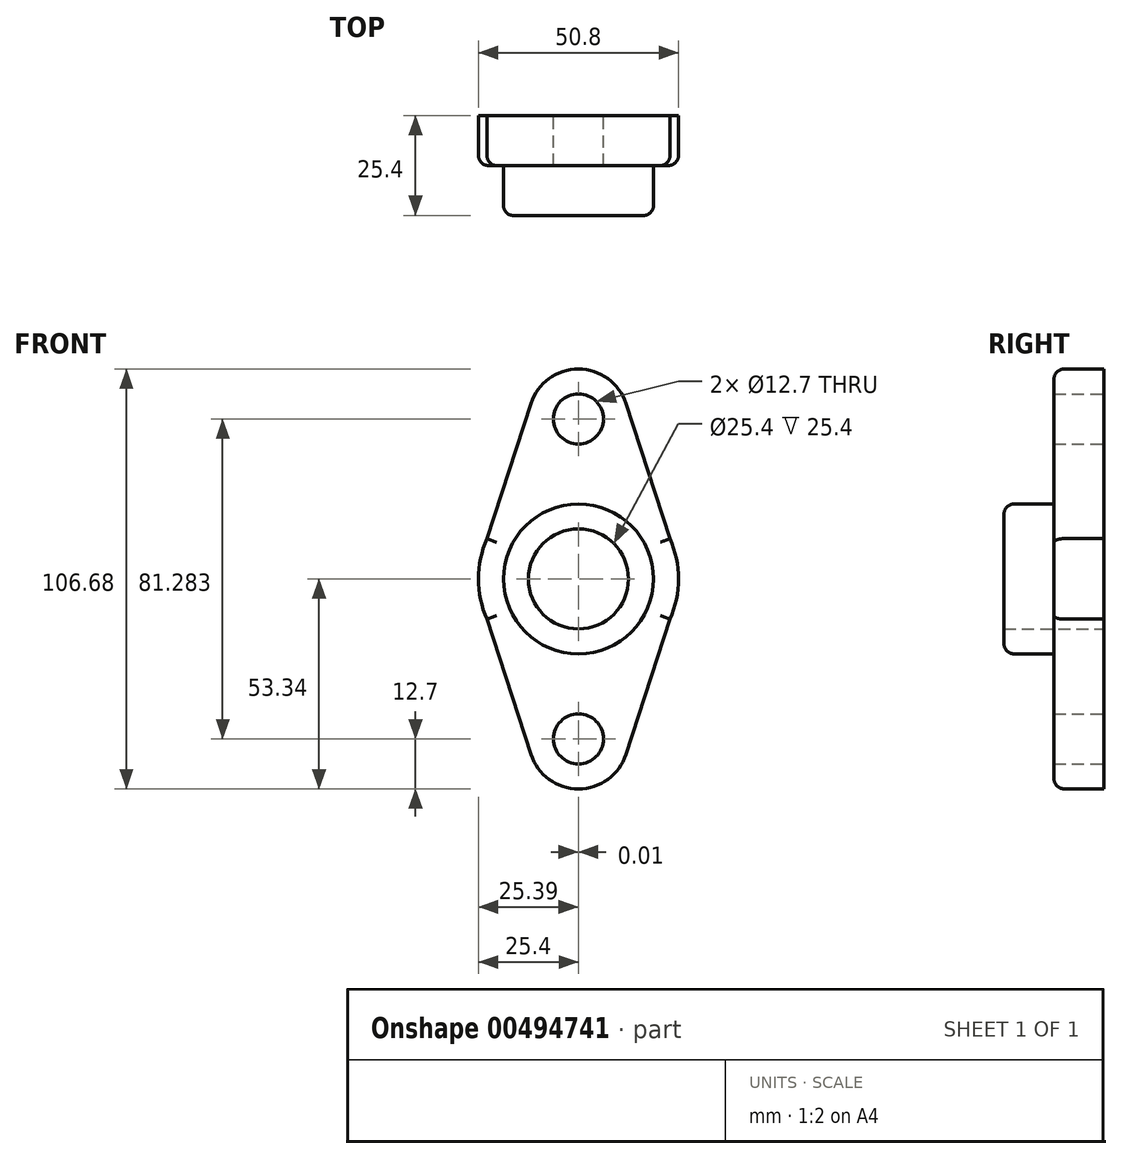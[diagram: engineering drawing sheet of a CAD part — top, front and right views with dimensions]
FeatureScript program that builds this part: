
annotation { "Feature Type Name" : "Feature", "Feature Type Description" : "" }
export const myFeature = defineFeature(function(context is Context, id is Id, definition is map)
    precondition{}
    {
        {
            var Q0;
            Q0=qCreatedBy(makeId("Front.planeOp"),FACE);
            var sketch = newSketch(context, id + "F0", { "sketchPlane" : qUnion([Q0])});
            skArc(sketch, "E0", {"start": v(23.25, -10.23) * mm, "mid": v(25.4, 0) * mm, "end": v(23.24, 10.25) * mm});
            skArc(sketch, "E1", {"start": v(12.07, 44.57) * mm, "mid": v(-0.01, 53.34) * mm, "end": v(-12.09, 44.57) * mm});
            skArc(sketch, "E2", {"start": v(-12.08, -44.57) * mm, "mid": v(0, -53.34) * mm, "end": v(12.08, -44.57) * mm});
            skLineSegment(sketch, "E3", {"start": v(-23.25, 10.22) * mm, "end": v(-12.09, 44.57) * mm});
            skLineSegment(sketch, "E4", {"start": v(23.24, 10.25) * mm, "end": v(12.07, 44.57) * mm});
            skLineSegment(sketch, "E5", {"start": v(-23.25, -10.23) * mm, "end": v(-12.08, -44.57) * mm});
            skLineSegment(sketch, "E6", {"start": v(23.25, -10.23) * mm, "end": v(12.08, -44.57) * mm});
            skCircle(sketch, "E7", {"center": v(-0.01, 40.64) * mm, "radius": 6.35 * mm});
            skCircle(sketch, "E8", {"center": v(0, -40.64) * mm, "radius": 6.35 * mm});
            skCircle(sketch, "E9", {"center": v(0, 0) * mm, "radius": 19.05 * mm});
            skCircle(sketch, "E10", {"center": v(0, 0) * mm, "radius": 12.7 * mm});
            skArc(sketch, "E11.trimOffspring", {"start": v(-23.25, 10.22) * mm, "mid": v(-25.4, 0) * mm, "end": v(-23.25, -10.23) * mm});
            skSolve(sketch);
        }
        {
            var Q0;
            Q0=makeQuery(id+"F0.imprint","IMPRINT",FACE,{"disambiguationData":[TD([[makeQuery(id+"F0.imprint","IMPRINT",EDGE,{"derivedFrom":sQuery(id+"F0.wireOp",EDGE,"E0")}),1.0]])]});
            extrude(context, id + "F1", {"entities" : qUnion([Q0]), "depth" : 12.7 * mm});
        }
        {
            var Q0;
            Q0=makeQuery(id+"F0.imprint","IMPRINT",FACE,{"disambiguationData":[TD([[makeQuery(id+"F0.imprint","IMPRINT",EDGE,{"derivedFrom":sQuery(id+"F0.wireOp",EDGE,"E9")}),1.0]])]});
            extrude(context, id + "F2", {"entities" : qUnion([Q0]), "operationType" : NewBodyOperationType.ADD, "depth" : 25.4 * mm});
        }
        {
            var Q0;
            Q0=makeQuery(id+"F1.opExtrude","CAP_EDGE",EDGE,{"disambiguationData":[OSD([sQuery(id+"F0.wireOp",EDGE,"E3")])],"isStart":false});
            var Q1;
            Q1=makeQuery(id+"F1.opExtrude","CAP_EDGE",EDGE,{"disambiguationData":[OSD([sQuery(id+"F0.wireOp",EDGE,"E1")])],"isStart":false});
            var Q2;
            Q2=makeQuery(id+"F1.opExtrude","CAP_EDGE",EDGE,{"disambiguationData":[OSD([sQuery(id+"F0.wireOp",EDGE,"E11.trimOffspring")])],"isStart":false});
            var Q3;
            Q3=makeQuery(id+"F1.opExtrude","CAP_EDGE",EDGE,{"disambiguationData":[OSD([sQuery(id+"F0.wireOp",EDGE,"E5")])],"isStart":false});
            var Q4;
            Q4=makeQuery(id+"F1.opExtrude","CAP_EDGE",EDGE,{"disambiguationData":[OSD([sQuery(id+"F0.wireOp",EDGE,"E2")])],"isStart":false});
            var Q5;
            Q5=makeQuery(id+"F1.opExtrude","CAP_EDGE",EDGE,{"disambiguationData":[OSD([sQuery(id+"F0.wireOp",EDGE,"E6")])],"isStart":false});
            var Q6;
            Q6=makeQuery(id+"F1.opExtrude","CAP_EDGE",EDGE,{"disambiguationData":[OSD([sQuery(id+"F0.wireOp",EDGE,"E0")])],"isStart":false});
            var Q7;
            Q7=makeQuery(id+"F1.opExtrude","CAP_EDGE",EDGE,{"disambiguationData":[OSD([sQuery(id+"F0.wireOp",EDGE,"E4")])],"isStart":false});
            fillet(context, id + "F3", {"entities" : qUnion([Q0, Q1, Q2, Q3, Q4, Q5, Q6, Q7]), "radius" : 2.54 * mm, "tangentPropagation" : true, "allowEdgeOverflow" : false});
        }
        {
            var Q0;
            Q0=makeQuery(id+"F2.opExtrude","CAP_EDGE",EDGE,{"disambiguationData":[OSD([sQuery(id+"F0.wireOp",EDGE,"E9")])],"isStart":false});
            fillet(context, id + "F4", {"entities" : qUnion([Q0]), "radius" : 2.54 * mm, "tangentPropagation" : true, "allowEdgeOverflow" : false});
        }
    });
